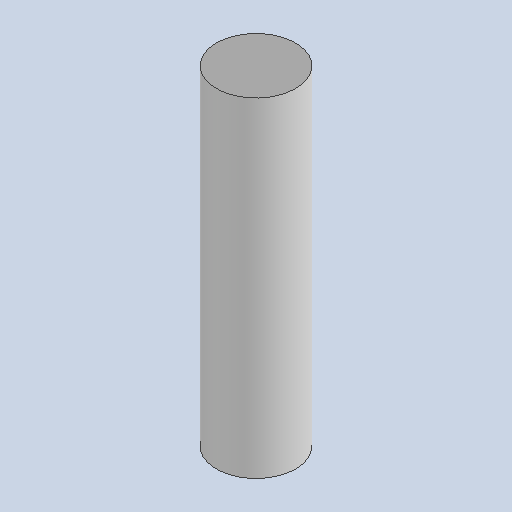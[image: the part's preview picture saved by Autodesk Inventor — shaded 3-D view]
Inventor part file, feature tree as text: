
AUTODESK INVENTOR PART (.ipt)
format: ipt  version: 2025 (Build 290162010, 162A)  size: 78,336 bytes
history: native  units: mm
features: extrude x1, sketch x1
ambient origin geometry x8: Origin, YZ Plane, XZ Plane, XY Plane, X Axis, Y Axis, Z Axis, Center Point
bodies: Solid1 (feature_tree)
feature tree (2):
  extrude  "Extrusion1"  Depth=50.0mm TaperAngle=0.0deg
  sketch  "Sketch1"  dims[d0=12.0mm d1=50.0mm d2=40.0mm d3=0.0mm d4=0.0mm]
